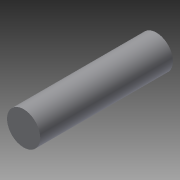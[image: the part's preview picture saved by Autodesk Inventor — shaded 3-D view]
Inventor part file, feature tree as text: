
AUTODESK INVENTOR PART (.ipt)
format: ipt  version: 2014 (Build 180170000, 170)  size: 70,656 bytes
history: native  units: in
note: dims shown in document units (in); Inventor stores cm internally (conversion verified against a paired STEP export)
features: extrude x1, sketch x1
ambient origin geometry x8: Origin, YZ Plane, XZ Plane, XY Plane, X Axis, Y Axis, Z Axis, Center Point
bodies: Solid1 (feature_tree)
feature tree (2):
  extrude  "Extrusion1"  Depth=1.0in TaperAngle=0.0deg
  sketch  "Sketch1"  dims[d0=0.25in d1=1.0in d2=0.0in]
